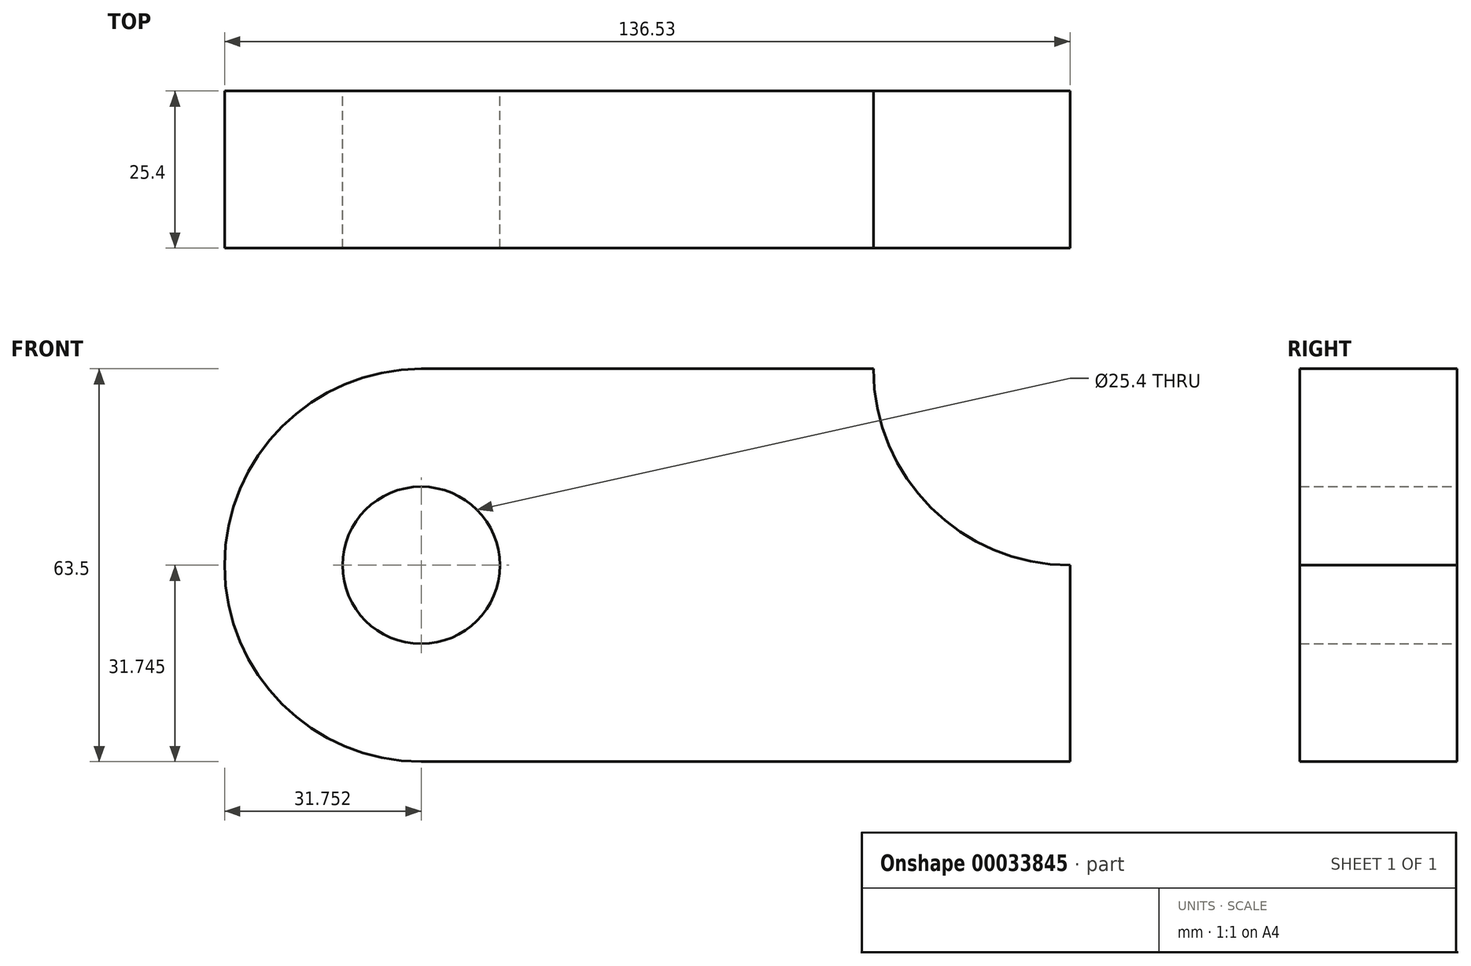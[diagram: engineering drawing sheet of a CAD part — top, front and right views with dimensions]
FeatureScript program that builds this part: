
annotation { "Feature Type Name" : "Feature", "Feature Type Description" : "" }
export const myFeature = defineFeature(function(context is Context, id is Id, definition is map)
    precondition{}
    {
        {
            var Q0;
            Q0=qCreatedBy(makeId("Front.planeOp"),FACE);
            var sketch = newSketch(context, id + "F0", { "sketchPlane" : qUnion([Q0])});
            skLineSegment(sketch, "E0.bottom", {"start": v(-75.53, 51) * mm, "end": v(29.25, 51) * mm});
            skLineSegment(sketch, "E0.top", {"start": v(-75.53, -12.5) * mm, "end": v(29.25, -12.5) * mm});
            skLineSegment(sketch, "E0.left", {"start": v(-75.53, 51) * mm, "end": v(-75.53, -12.5) * mm});
            skLineSegment(sketch, "E0.right", {"start": v(29.25, 51) * mm, "end": v(29.25, -12.5) * mm});
            skCircle(sketch, "E1", {"center": v(-75.53, 19.25) * mm, "radius": 31.75 * mm});
            skCircle(sketch, "E2", {"center": v(-75.53, 19.25) * mm, "radius": 12.7 * mm});
            skCircle(sketch, "E3", {"center": v(29.25, 51) * mm, "radius": 31.75 * mm});
            skSolve(sketch);
        }
        {
            var Q0;
            {var subQ0=sQuery(id+"F0.wireOp",EDGE,"E2");var subQ1=sQuery(id+"F0.wireOp",EDGE,"E0.left");var subQ3=makeQuery(id+"F0.imprint","INTERSECT",VERTEX,{"disambiguationData":[OD(0.0)],"derivedFrom":[subQ1,subQ0]});Q0=makeQuery(id+"F0.imprint","IMPRINT",FACE,{"disambiguationData":[TD([[makeQuery(id+"F0.imprint","IMPRINT",EDGE,{"disambiguationData":[TD([[subQ3,1.0]])],"derivedFrom":subQ0}),-1.0]])]});}
            var Q1;
            {var subQ0=sQuery(id+"F0.wireOp",EDGE,"E2");var subQ1=sQuery(id+"F0.wireOp",EDGE,"E0.left");var subQ3=makeQuery(id+"F0.imprint","INTERSECT",VERTEX,{"disambiguationData":[OD(0.0)],"derivedFrom":[subQ1,subQ0]});Q1=makeQuery(id+"F0.imprint","IMPRINT",FACE,{"disambiguationData":[TD([[makeQuery(id+"F0.imprint","IMPRINT",EDGE,{"disambiguationData":[TD([[subQ3,-1.0]])],"derivedFrom":subQ0}),-1.0]])]});}
            var Q2;
            {var subQ6=sQuery(id+"F0.wireOp",EDGE,"E0.top");Q2=makeQuery(id+"F0.imprint","IMPRINT",FACE,{"disambiguationData":[TD([[makeQuery(id+"F0.imprint","IMPRINT",EDGE,{"derivedFrom":subQ6}),1.0]])]});}
            extrude(context, id + "F1", {"entities" : qUnion([Q0, Q1, Q2]), "depth" : 25.4 * mm});
        }
    });
